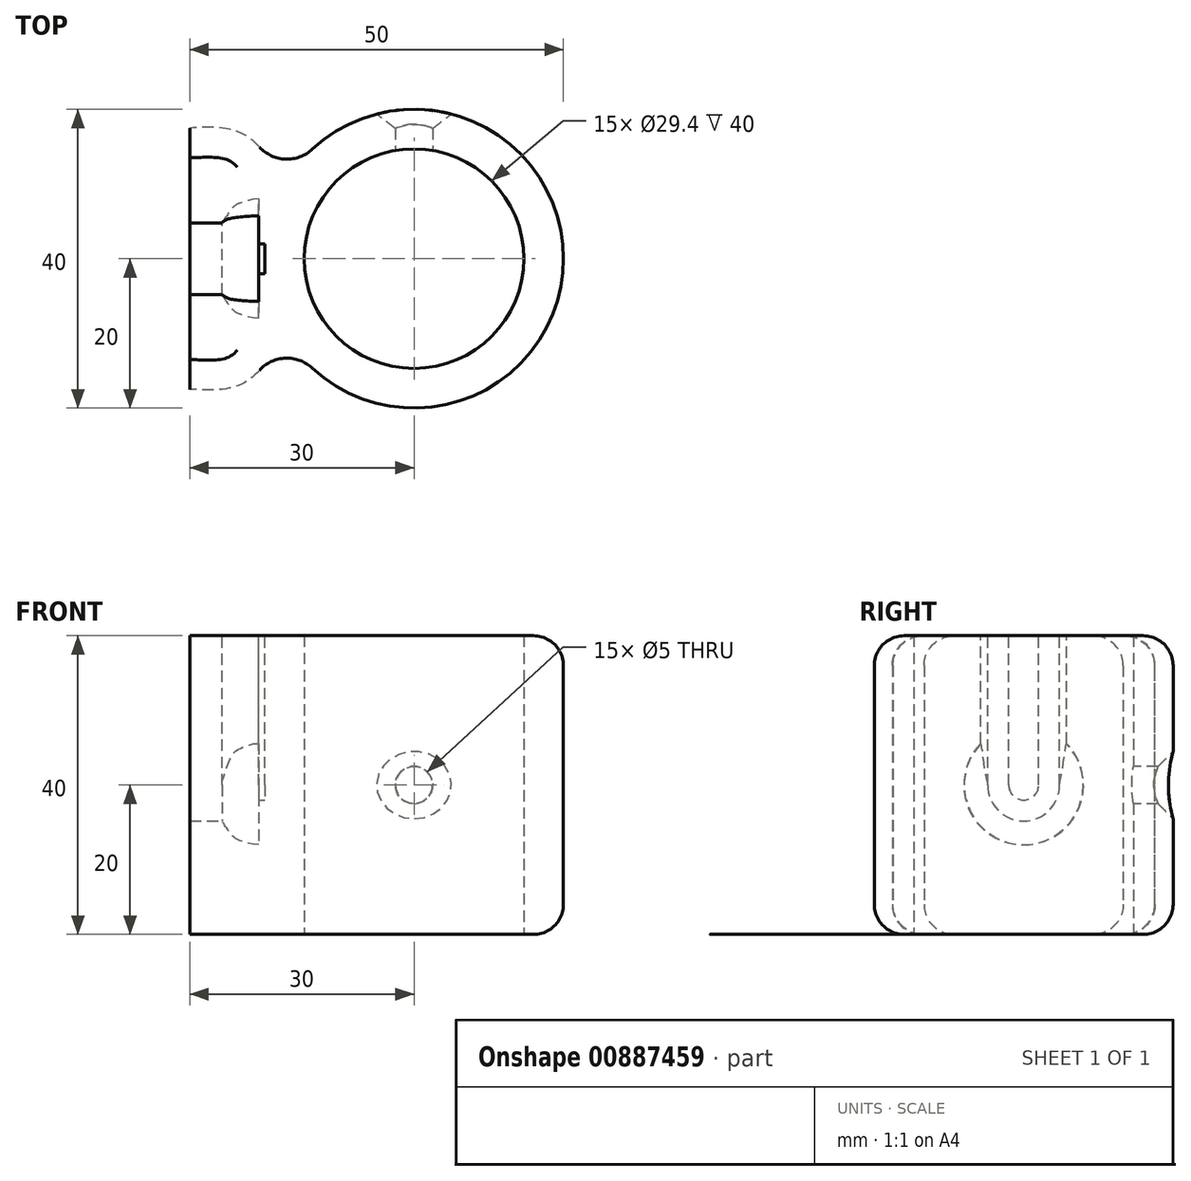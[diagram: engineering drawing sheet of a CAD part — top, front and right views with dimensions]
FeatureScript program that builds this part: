
annotation { "Feature Type Name" : "Feature", "Feature Type Description" : "" }
export const myFeature = defineFeature(function(context is Context, id is Id, definition is map)
    precondition{}
    {
        {
            var Q0;
            Q0=qCreatedBy(makeId("Top.planeOp"),FACE);
            var sketch = newSketch(context, id + "F0", { "sketchPlane" : qUnion([Q0])});
            skCircle(sketch, "E0", {"center": v(0, 0) * mm, "radius": 14.7 * mm});
            skArc(sketch, "E1", {"start": v(-17.32, -10) * mm, "mid": v(20, 0) * mm, "end": v(-17.32, 10) * mm});
            skLineSegment(sketch, "E2", {"start": v(-30, 17.5) * mm, "end": v(-30, -17.5) * mm});
            skPoint(sketch, "E3", {"position": v(-30, 0) * mm});
            skFitSpline(sketch, "E4", {"points": [v(-30, -17.5) * mm, v(-22.77, -16.63) * mm, v(-17.32, -10) * mm], "startDerivative": vector(16.19, -0.81) * mm, "endDerivative": vector(9.26, 15.6) * mm});
            skFitSpline(sketch, "E5.MirrorCS", {"points": [v(-30, 17.5) * mm, v(-22.77, 16.63) * mm, v(-17.32, 10) * mm], "startDerivative": vector(16.19, 0.81) * mm, "endDerivative": vector(9.26, -15.6) * mm});
            skSolve(sketch);
        }
        {
            var Q0;
            Q0=makeQuery(id+"F0.imprint","IMPRINT",FACE,{"disambiguationData":[TD([[makeQuery(id+"F0.imprint","IMPRINT",EDGE,{"derivedFrom":sQuery(id+"F0.wireOp",EDGE,"E0")}),-1.0]])]});
            extrude(context, id + "F1", {"entities" : qUnion([Q0]), "depth" : 40 * mm, "offsetDistance" : 25 * mm});
        }
        {
            var Q0;
            Q0=makeQuery(id+"F1.opExtrude","CAP_FACE",FACE,{"disambiguationData":[OSD([sQuery(id+"F0.wireOp",EDGE,"E0"),sQuery(id+"F0.wireOp",EDGE,"E1"),sQuery(id+"F0.wireOp",EDGE,"E2"),sQuery(id+"F0.wireOp",EDGE,"E4"),sQuery(id+"F0.wireOp",EDGE,"E5.MirrorCS")])],"isStart":false});
            var sketch = newSketch(context, id + "F2", { "sketchPlane" : qUnion([Q0])});
            skLineSegment(sketch, "E6", {"start": v(-30, 0) * mm, "end": v(-30, 4.8) * mm});
            skLineSegment(sketch, "E7", {"start": v(-30, 4.8) * mm, "end": v(-25.7, 4.8) * mm});
            skLineSegment(sketch, "E8", {"start": v(-20.8, 5.75) * mm, "end": v(-20.8, 0) * mm, "construction": true});
            skLineSegment(sketch, "E9", {"start": v(-20, 0) * mm, "end": v(-20, 2) * mm});
            skLineSegment(sketch, "E10", {"start": v(-20, 2) * mm, "end": v(-20.8, 2) * mm});
            skLineSegment(sketch, "E11", {"start": v(-20.8, 2) * mm, "end": v(-20.8, 5.75) * mm});
            skLineSegment(sketch, "E12.MirrorCS", {"start": v(-20, -2) * mm, "end": v(-20.8, -2) * mm});
            skLineSegment(sketch, "E13.MirrorCS", {"start": v(-20.8, -2) * mm, "end": v(-20.8, -5.75) * mm});
            skLineSegment(sketch, "E14.MirrorCS", {"start": v(-20.8, -5.75) * mm, "end": v(-20.8, 0) * mm, "construction": true});
            skLineSegment(sketch, "E15.MirrorCS", {"start": v(-20, 0) * mm, "end": v(-20, -2) * mm});
            skLineSegment(sketch, "E16.MirrorCS", {"start": v(-30, -4.8) * mm, "end": v(-25.7, -4.8) * mm});
            skLineSegment(sketch, "E17.MirrorCS", {"start": v(-30, 0) * mm, "end": v(-30, -4.8) * mm});
            skFitSpline(sketch, "E18", {"points": [v(-25.7, 4.8) * mm, v(-24.95, 5.29) * mm, v(-20.8, 5.75) * mm], "startDerivative": vector(1.8, 1.68) * mm, "endDerivative": vector(7.33, 0.38) * mm});
            skFitSpline(sketch, "E19.MirrorCS", {"points": [v(-25.7, -4.8) * mm, v(-24.95, -5.29) * mm, v(-20.8, -5.75) * mm], "startDerivative": vector(1.8, -1.68) * mm, "endDerivative": vector(7.33, -0.38) * mm});
            skSolve(sketch);
        }
        {
            var Q0;
            Q0 = qSketchRegion(id + "F2", true);
            extrude(context, id + "F3", {"entities" : qUnion([Q0]), "operationType" : NewBodyOperationType.REMOVE, "oppositeDirection" : true, "depth" : 20 * mm, "offsetDistance" : 25 * mm});
        }
        {
            var Q0;
            Q0=makeQuery(id+"F3.boolean.opBoolean","COPY",FACE,{"derivedFrom":makeQuery(id+"F3.opExtrude","CAP_FACE",FACE,{"disambiguationData":[OSD([sQuery(id+"F2.wireOp",EDGE,"E6"),sQuery(id+"F2.wireOp",EDGE,"E7"),sQuery(id+"F2.wireOp",EDGE,"ZKGljO8y-MB6T-8WGz-cBIm-B1j7Zv4u35g7"),sQuery(id+"F2.wireOp",EDGE,"E9"),sQuery(id+"F2.wireOp",EDGE,"E10"),sQuery(id+"F2.wireOp",EDGE,"E11"),sQuery(id+"F2.wireOp",EDGE,"E12.MirrorCS"),sQuery(id+"F2.wireOp",EDGE,"E13.MirrorCS"),sQuery(id+"F2.wireOp",EDGE,"eb95d0b8-e14f-4264-a8f6-f16cf73518472.MirrorCS"),sQuery(id+"F2.wireOp",EDGE,"E15.MirrorCS"),sQuery(id+"F2.wireOp",EDGE,"E16.MirrorCS"),sQuery(id+"F2.wireOp",EDGE,"E17.MirrorCS")])],"isStart":false})});
            var sketch = newSketch(context, id + "F4", { "sketchPlane" : qUnion([Q0])});
            skLineSegment(sketch, "E20", {"start": v(-20, 0) * mm, "end": v(-20, 2) * mm});
            skLineSegment(sketch, "E21", {"start": v(-20, 2) * mm, "end": v(-20.8, 2) * mm});
            skLineSegment(sketch, "E22", {"start": v(-20.8, 2) * mm, "end": v(-20.8, 8) * mm});
            skLineSegment(sketch, "E23", {"start": v(-25.7, 4.8) * mm, "end": v(-30, 4.8) * mm});
            skLineSegment(sketch, "E24", {"start": v(-30, 4.8) * mm, "end": v(-30, 0) * mm});
            skLineSegment(sketch, "E25", {"start": v(-33.08, 0) * mm, "end": v(-15.81, 0) * mm, "construction": true});
            skLineSegment(sketch, "E26", {"start": v(-20, 0) * mm, "end": v(-30, 0) * mm});
            skFitSpline(sketch, "E27", {"points": [v(-25.7, 4.8) * mm, v(-24.36, 6.75) * mm, v(-23.18, 7.47) * mm, v(-20.8, 8) * mm], "startDerivative": vector(2.78, 3.73) * mm, "endDerivative": vector(7.3, -0.03) * mm});
            skSolve(sketch);
        }
        {
            var Q0;
            Q0 = qSketchRegion(id + "F4", true);
            var Q1;
            Q1=sQuery(id+"F4.wireOp",EDGE,"E25");
            revolve(context, id + "F5", {"operationType" : NewBodyOperationType.REMOVE, "surfaceOperationType" : NewSurfaceOperationType.NEW, "entities" : qUnion([Q0]), "axis" : qUnion([Q1]), "revolveType" : RevolveType.FULL, "oppositeDirection" : true});
        }
        {
            var Q0;
            Q0=makeQuery(id+"F1.opExtrude","SWEPT_EDGE",EDGE,{"disambiguationData":[OSD([sQuery(id+"F0.wireOp",EDGE,"E1"),sQuery(id+"F0.wireOp",EDGE,"E4")])]});
            var Q1;
            Q1=makeQuery(id+"F1.opExtrude","SWEPT_EDGE",EDGE,{"disambiguationData":[OSD([sQuery(id+"F0.wireOp",EDGE,"E1"),sQuery(id+"F0.wireOp",EDGE,"E5.MirrorCS")])]});
            fillet(context, id + "F6", {"entities" : qUnion([Q0, Q1]), "radius" : 5 * mm, "tangentPropagation" : true, "allowEdgeOverflow" : false});
        }
        {
            var Q0;
            Q0=makeQuery(id+"F1.opExtrude","CAP_EDGE",EDGE,{"disambiguationData":[OSD([sQuery(id+"F0.wireOp",EDGE,"E1")])],"isStart":false});
            var Q1;
            Q1=makeQuery(id+"F1.opExtrude","CAP_EDGE",EDGE,{"disambiguationData":[OSD([sQuery(id+"F0.wireOp",EDGE,"E1")])],"isStart":true});
            fillet(context, id + "F7", {"entities" : qUnion([Q0, Q1]), "radius" : 4 * mm, "tangentPropagation" : true, "allowEdgeOverflow" : false});
        }
        {
            var Q0;
            Q0=qCreatedBy(makeId("Front.planeOp"),FACE);
            cPlane(context, id + "F8", {"entities" : qUnion([Q0]), "cplaneType" : CPlaneType.OFFSET, "offset" : 10 * mm, "oppositeDirection" : true, "width" : 150 * mm, "height" : 150 * mm});
        }
        {
            var Q0;
            Q0=qCreatedBy(id+"F8.planeOp",FACE);
            var sketch = newSketch(context, id + "F9", { "sketchPlane" : qUnion([Q0])});
            skLineSegment(sketch, "E28", {"start": v(0, 0) * mm, "end": v(0, 40) * mm, "construction": true});
            skCircle(sketch, "E29", {"center": v(0, 20) * mm, "radius": 2.5 * mm});
            skSolve(sketch);
        }
        {
            var Q0;
            Q0 = qSketchRegion(id + "F9", true);
            extrude(context, id + "F10", {"entities" : qUnion([Q0]), "operationType" : NewBodyOperationType.REMOVE, "oppositeDirection" : true, "depth" : 11 * mm, "offsetDistance" : 25 * mm});
        }
        {
            var Q0;
            Q0=makeQuery(id+"F10.boolean.opBoolean","INTERSECT",EDGE,{"derivedFrom":[makeQuery(id+"F1.opExtrude","SWEPT_FACE",FACE,{"disambiguationData":[OSD([sQuery(id+"F0.wireOp",EDGE,"E1")])]}),makeQuery(id+"F10.opExtrude","SWEPT_FACE",FACE,{"disambiguationData":[OSD([sQuery(id+"F9.wireOp",EDGE,"E29")])]})]});
            chamfer(context, id + "F11", {"entities" : qUnion([Q0]), "width" : 2 * mm, "tangentPropagation" : true});
        }
    });
